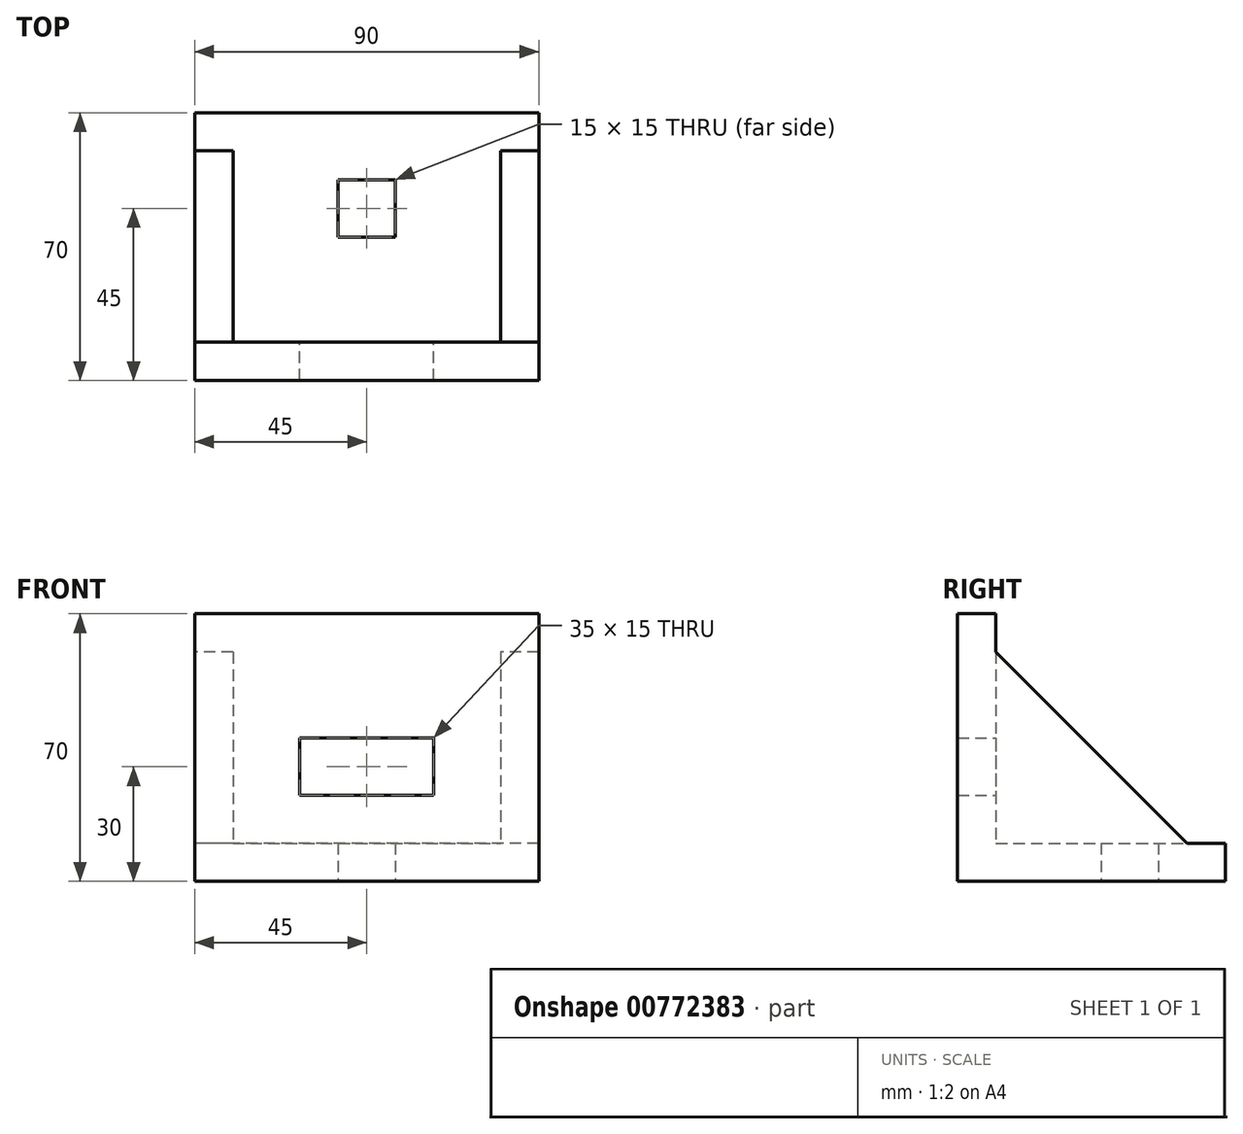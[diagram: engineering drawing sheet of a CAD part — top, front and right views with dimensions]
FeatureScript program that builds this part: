
annotation { "Feature Type Name" : "Feature", "Feature Type Description" : "" }
export const myFeature = defineFeature(function(context is Context, id is Id, definition is map)
    precondition{}
    {
        {
            var Q0;
            Q0=qCreatedBy(makeId("Right.planeOp"),FACE);
            var sketch = newSketch(context, id + "F0", { "sketchPlane" : qUnion([Q0])});
            skLineSegment(sketch, "E0", {"start": v(0, 0) * mm, "end": v(0, 70) * mm});
            skLineSegment(sketch, "E1", {"start": v(0, 70) * mm, "end": v(10, 70) * mm});
            skLineSegment(sketch, "E2", {"start": v(10, 70) * mm, "end": v(10, 60) * mm});
            skLineSegment(sketch, "E3", {"start": v(10, 60) * mm, "end": v(60, 10) * mm});
            skLineSegment(sketch, "E4", {"start": v(60, 10) * mm, "end": v(70, 10) * mm});
            skLineSegment(sketch, "E5", {"start": v(70, 10) * mm, "end": v(70, 0) * mm});
            skLineSegment(sketch, "E6", {"start": v(70, 0) * mm, "end": v(0, 0) * mm});
            skLineSegment(sketch, "E7", {"start": v(10, 60) * mm, "end": v(10, 10) * mm});
            skLineSegment(sketch, "E8", {"start": v(10, 10) * mm, "end": v(60, 10) * mm});
            skLineSegment(sketch, "E9", {"start": v(0, 37.5) * mm, "end": v(10, 37.5) * mm});
            skLineSegment(sketch, "E10", {"start": v(0, 22.5) * mm, "end": v(10, 22.5) * mm});
            skLineSegment(sketch, "E11", {"start": v(37.5, 10) * mm, "end": v(37.5, 0) * mm});
            skLineSegment(sketch, "E12", {"start": v(52.5, 10) * mm, "end": v(52.5, 0) * mm});
            skLineSegment(sketch, "E13", {"start": v(5, 37.5) * mm, "end": v(5, 22.5) * mm, "construction": true});
            skPoint(sketch, "E14", {"position": v(5, 30) * mm});
            skLineSegment(sketch, "E15", {"start": v(37.5, 5) * mm, "end": v(52.5, 5) * mm, "construction": true});
            skPoint(sketch, "E16", {"position": v(45, 5) * mm});
            skSolve(sketch);
        }
        {
            var Q0;
            {var subQ3=sQuery(id+"F0.wireOp",EDGE,"E1");Q0=makeQuery(id+"F0.imprint","IMPRINT",FACE,{"disambiguationData":[TD([[makeQuery(id+"F0.imprint","IMPRINT",EDGE,{"derivedFrom":subQ3}),-1.0]])]});}
            var Q1;
            {var subQ0=sQuery(id+"F0.wireOp",EDGE,"E9");Q1=makeQuery(id+"F0.imprint","IMPRINT",FACE,{"disambiguationData":[TD([[makeQuery(id+"F0.imprint","IMPRINT",EDGE,{"derivedFrom":subQ0}),-1.0]])]});}
            var Q2;
            {var subQ4=sQuery(id+"F0.wireOp",EDGE,"E10");Q2=makeQuery(id+"F0.imprint","IMPRINT",FACE,{"disambiguationData":[TD([[makeQuery(id+"F0.imprint","IMPRINT",EDGE,{"derivedFrom":subQ4}),-1.0]])]});}
            var Q3;
            {var subQ5=sQuery(id+"F0.wireOp",EDGE,"E3");Q3=makeQuery(id+"F0.imprint","IMPRINT",FACE,{"disambiguationData":[TD([[makeQuery(id+"F0.imprint","IMPRINT",EDGE,{"derivedFrom":subQ5}),-1.0]])]});}
            var Q4;
            {var subQ0=sQuery(id+"F0.wireOp",EDGE,"E11");Q4=makeQuery(id+"F0.imprint","IMPRINT",FACE,{"disambiguationData":[TD([[makeQuery(id+"F0.imprint","IMPRINT",EDGE,{"derivedFrom":subQ0}),1.0]])]});}
            var Q5;
            {var subQ4=sQuery(id+"F0.wireOp",EDGE,"E4");Q5=makeQuery(id+"F0.imprint","IMPRINT",FACE,{"disambiguationData":[TD([[makeQuery(id+"F0.imprint","IMPRINT",EDGE,{"derivedFrom":subQ4}),-1.0]])]});}
            extrude(context, id + "F1", {"entities" : qUnion([Q0, Q1, Q2, Q3, Q4, Q5]), "endBound" : BoundingType.SYMMETRIC, "depth" : 90 * mm, "offsetDistance" : 25 * mm});
        }
        {
            var Q0;
            {var subQ5=sQuery(id+"F0.wireOp",EDGE,"E3");Q0=makeQuery(id+"F0.imprint","IMPRINT",FACE,{"disambiguationData":[TD([[makeQuery(id+"F0.imprint","IMPRINT",EDGE,{"derivedFrom":subQ5}),-1.0]])]});}
            extrude(context, id + "F2", {"entities" : qUnion([Q0]), "operationType" : NewBodyOperationType.REMOVE, "endBound" : BoundingType.SYMMETRIC, "oppositeDirection" : true, "depth" : (90 - 20) * mm, "offsetDistance" : 25 * mm});
        }
        {
            var Q0;
            {var subQ0=sQuery(id+"F0.wireOp",EDGE,"E9");Q0=makeQuery(id+"F0.imprint","IMPRINT",FACE,{"disambiguationData":[TD([[makeQuery(id+"F0.imprint","IMPRINT",EDGE,{"derivedFrom":subQ0}),-1.0]])]});}
            extrude(context, id + "F3", {"entities" : qUnion([Q0]), "operationType" : NewBodyOperationType.REMOVE, "endBound" : BoundingType.SYMMETRIC, "depth" : 35 * mm, "offsetDistance" : 25 * mm});
        }
        {
            var Q0;
            {var subQ0=sQuery(id+"F0.wireOp",EDGE,"E11");Q0=makeQuery(id+"F0.imprint","IMPRINT",FACE,{"disambiguationData":[TD([[makeQuery(id+"F0.imprint","IMPRINT",EDGE,{"derivedFrom":subQ0}),1.0]])]});}
            extrude(context, id + "F4", {"entities" : qUnion([Q0]), "operationType" : NewBodyOperationType.REMOVE, "endBound" : BoundingType.SYMMETRIC, "oppositeDirection" : true, "depth" : 15 * mm, "offsetDistance" : 25 * mm});
        }
    });
